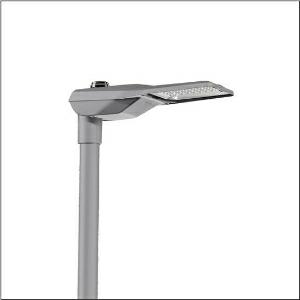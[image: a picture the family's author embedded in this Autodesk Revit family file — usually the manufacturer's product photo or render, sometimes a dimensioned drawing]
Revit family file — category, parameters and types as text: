
# Revit family: streetlight_sl_21_mini___p1_0a_5xe6a47n08hb_abf4
name_source: partatom
category: Lighting Fixtures
units: mm (PartAtom-declared; Revit-internal decimal feet)

## family parameters
Cut with Voids When Loaded = No
Host = Face
Light Source = No
Part Type = Normal
Room Calculation Point = No
Round Connector Dimension = Use Diameter
Shared = No

## types (1)
- --- (1 x LED, 9430 lm, 66 W, 4000K)
    Apparent Load = 66 VA
    CIE Flux Codes = 21 50 90 100 100
    Color Rendering = 70
    Color Temperature = 4000K
    Default Elevation = 1800 mm
    Description = Streetlight SL 21 mini, mast luminaire, primary light control with lens, of PMMA, primary optical cover: cover, of toughened safety glass, transparent, light distribution: P1.0a, light emission: direct distribution, primary light characteristic: asymmetric, installation type: side-entry, LED, 3G 1.5mm², High Power LED, rated luminous flux: 9.430lm, luminous efficacy: 143lm/W, light colour: 740, colour temperature: 4000K, control gear: NEMA (7pin), control: overheat protection, pre-setting: linear dimming characteristic, constant luminous flux control, time-dependent luminous flux control, flexible luminous flux parameterisation, mains connection: 230..240V, AC, 50/60Hz, connection cable pre-assembled, cable length: 8,5m, wiring characteristics: H07RN-F, start of lifetime: 66W, end of service life: 69W, reduction: 30W, luminaire housing, of diecast aluminium (EN AC-44300), powder-coated, Siteco® metallic grey (DB 702S), corrosivity category C5 mid according to DIN EN ISO 12944, multi-level sealing system, sealing non-destructively replaceable, inclination adjustable: 0°, 5°, 10°, 15°, length: 628mm, width: 235mm, height: 110mm, spigot size: 42mm (side-entry), mounting height: 4..8m, protection rating (complete): IP66, insulation class (complete): insulation class I (protective earthing), certification: CE, ENEC, ENEC+, VDE, impact resistance: IK10, permissible operating ambient temperature for outdoor applications: -40..+50°C, standard-compliant lighting for roads and squares, packaging unit: 1 piece

Light Distribution: P1.0a
    Height = 110 mm
    Lamp = 1 x LED
    Lamp Light Flux = 9430 lm
    Lamp Power = 66 W
    Lamp count = 1
    Length = 625 mm
    Luminous efficacy = 143 lm/W
    Manufacturer = Siteco
    ModVariant = No
    Model = 5XE6A47N08HB
    Number of Poles = 1
    OnlyDefault = Yes
    Power Factor = 1
    Product Name = Streetlight SL 21 mini | P1.0a
    Product group = mast luminaire | pylon top
    ProductGroupID = 6100
    Protection Class = Protection class I
    Protection Degree = IP 66
    RLX_Detail_Level = 1
    RLX_Emergency_Light_Flux = 0 lm
    RLX_Emergency_Type = 0
    RLX_Emergency_Type_DB = No
    RlxData = <blob elided: 37341 chars, md5=5335627d>
    Socket = socket
    Standby Power = 0 W
    System Light Flux = 9430 lm
    System Power = 66 W
    Type Comments = factory setting: luminous flux: 100 % | dim-lin: 254 | 670 mA
    Type Image = l_1294379.jpg
    URL = http://relux.com
    VarID = @adj_156079
    Voltage = 0 V
    Weight = 0.00 kg
    Width = 234 mm

## geometry (parser evidence)
native form markers: Blend x4, Sweep x12
no freeform markers — native parametric forms only
